# Revit family: Sanitary_Toilet-Accessories_DURAVIT-AG_Karree-Brush-set-95x95x350-mm-009957ed
name_source: partatom
category: Generic Models
revit_build: Autodesk Revit 2018 (Build: 20190510_1515(x64)
units: mm (PartAtom-declared; Revit-internal decimal feet)

## family parameters
Can host rebar = No
Cut with Voids When Loaded = No
Host = Face
OmniClass Number = 23.31.25.00
OmniClass Title = Toilet and Bath Specialties
Part Type = Normal
Room Calculation Point = No
Round Connector Dimension = Use Diameter
Shared = No

## types (1)
- Karree Brush set 95x95x350 mm - 009957
    BIMobject category = Toilet Accessories
    Default Elevation = 1219 mm
    Description = Duravit Karree Brush set Chrome 95x95x350 mm - 0099571000
    Design country = Germany
    Details material = Duravit - Plastic - Dark Grey Plastic
    ETIM classification = EC010555 | Lavatory brush set
    Edition number = 1
    IFC Classification = Furnishing Element
    Installation instructions = https://duravit-public-assets.s3.eu-central-1.amazonaws.com
    Main material = Duravit - Metal - 10 - Chrome
    Manufacturer = Duravit
    Manufacturer name = DURAVIT AG
    Masterformat 2014 Code = 10 28 00
    Masterformat 2014 Description = Toilet, Bath, and Laundry Accessories
    Material main = Chrome
    Material secondary = Glass
    Model = Karree Brush set 95x95x350 mm - 009957
    OmniClass Code = 23-31 25 00
    OmniClass Description = Toilet and Bath Specialties
    Product Guid = f1e7930b-5084-4ed9-87fa-8629ff08e6fc
    Product SKU = Karree-Brush-set-95x95x350-mm-009957
    Product certification = http://pro.duravit.com
    Product data url = https://bimobject.com
    Product family = Karree
    Product group = Brush set
    Product name = Karree Brush set 95x95x350 mm - 009957
    Product url = http://pro.duravit.com
    QR code = https://bimobject.com
    Secondary material = Duravit - Glass - Frosted
    Technical description = http://pro.duravit.com
    UNSPSC Code = 301815
    URL = https://www.duravit.com
    Uniclass 2015 Code = Pr_40_20_76_86
    Uniclass 2015 Name = Toilet brush holders
    Uniformat II Code = E2010
    Uniformat II Description = Fixed Furnishings
    Weight Net (Kg) = 1,5
    Youtube clip = http://pro.duravit.com

## geometry (parser evidence)
native form markers: Sweep x4
no freeform markers — native parametric forms only
